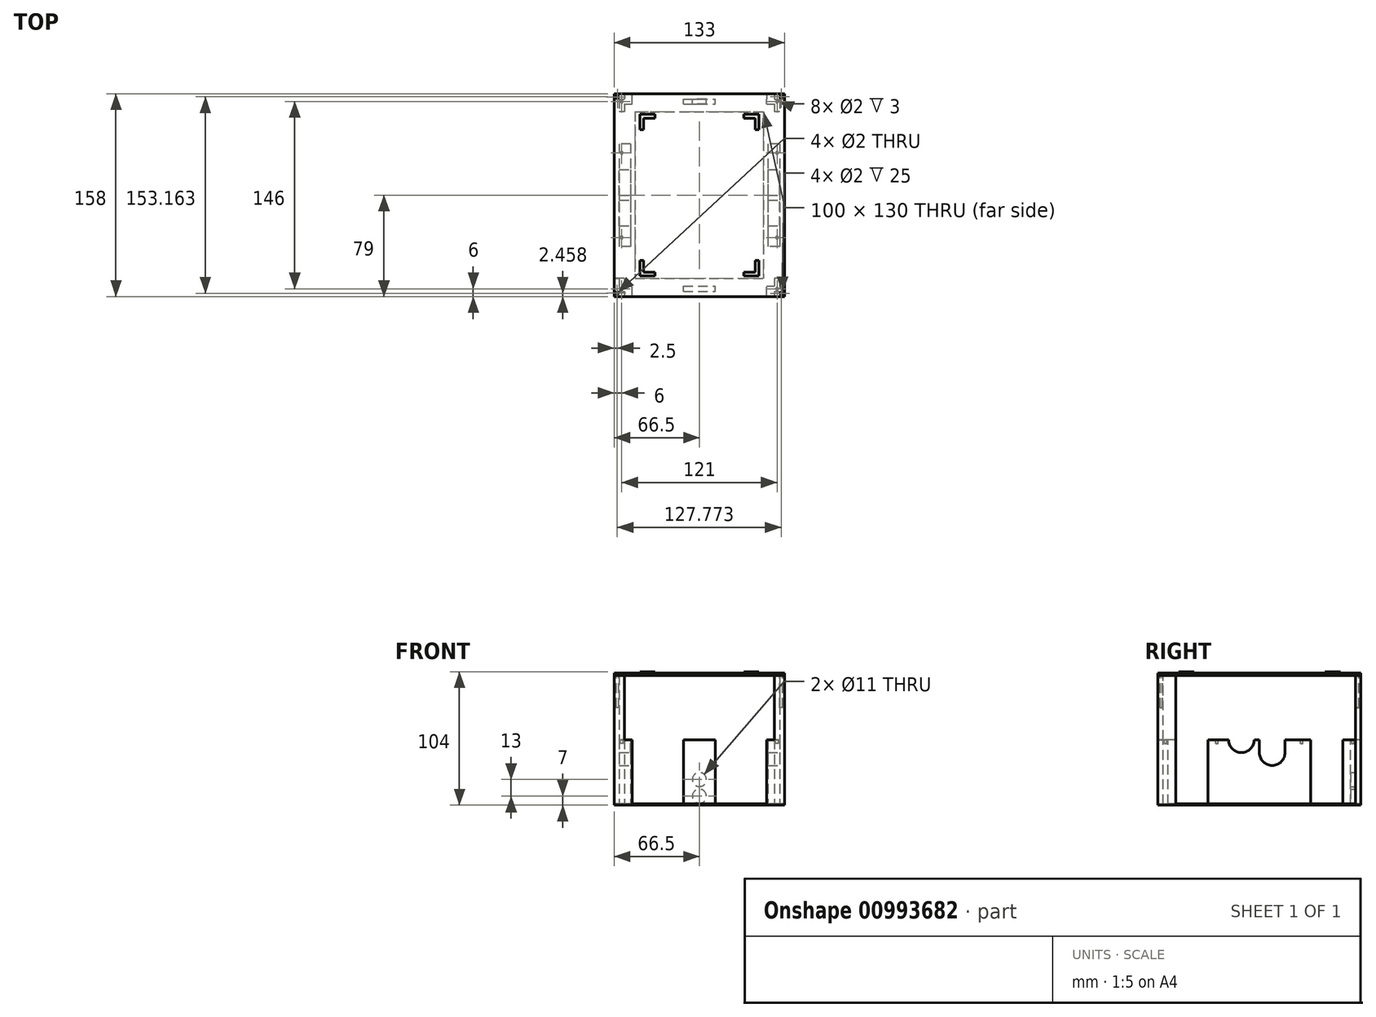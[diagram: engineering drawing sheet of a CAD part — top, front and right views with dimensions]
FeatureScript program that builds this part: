
annotation { "Feature Type Name" : "Feature", "Feature Type Description" : "" }
export const myFeature = defineFeature(function(context is Context, id is Id, definition is map)
    precondition{}
    {
        {
            var Q0;
            Q0=qCreatedBy(makeId("Top.planeOp"),FACE);
            var sketch = newSketch(context, id + "F0", { "sketchPlane" : qUnion([Q0])});
            skLineSegment(sketch, "E0.bottom", {"start": v(-66.5, 79) * mm, "end": v(66.5, 79) * mm});
            skLineSegment(sketch, "E0.top", {"start": v(-66.5, -79) * mm, "end": v(66.5, -79) * mm});
            skLineSegment(sketch, "E0.left", {"start": v(-66.5, 79) * mm, "end": v(-66.5, -79) * mm});
            skLineSegment(sketch, "E0.right", {"start": v(66.5, 79) * mm, "end": v(66.5, -79) * mm});
            skPoint(sketch, "E0.middle", {"position": v(0, 0) * mm});
            skLineSegment(sketch, "E1.bottom", {"start": v(-66.5, 79) * mm, "end": v(-66.5, 79) * mm});
            skLineSegment(sketch, "E1.top", {"start": v(-66.5, 79) * mm, "end": v(-66.5, 79) * mm});
            skLineSegment(sketch, "E1.left", {"start": v(-66.5, 79) * mm, "end": v(-66.5, 79) * mm});
            skLineSegment(sketch, "E1.right", {"start": v(-66.5, 79) * mm, "end": v(-66.5, 79) * mm});
            skLineSegment(sketch, "E2.bottom", {"start": v(-66.5, 79) * mm, "end": v(-62.5, 79) * mm});
            skLineSegment(sketch, "E2.top", {"start": v(-66.5, 79) * mm, "end": v(-62.5, 79) * mm});
            skLineSegment(sketch, "E2.right", {"start": v(-62.5, 79) * mm, "end": v(-62.5, 79) * mm});
            skSolve(sketch);
        }
        {
            var Q0;
            Q0=makeQuery(id+"F0.imprint","IMPRINT",FACE,{"disambiguationData":[TD([[makeQuery(id+"F0.imprint","IMPRINT",EDGE,{"derivedFrom":sQuery(id+"F0.wireOp",EDGE,"E0.bottom")}),-1.0]])]});
            extrude(context, id + "F1", {"entities" : qUnion([Q0]), "depth" : 1 * mm});
        }
        {
            var Q0;
            Q0=makeQuery(id+"F1.opExtrude","CAP_FACE",FACE,{"disambiguationData":[OSD([sQuery(id+"F0.wireOp",EDGE,"E0.bottom"),sQuery(id+"F0.wireOp",EDGE,"E0.top"),sQuery(id+"F0.wireOp",EDGE,"E0.left"),sQuery(id+"F0.wireOp",EDGE,"E0.right")])],"isStart":false});
            var sketch = newSketch(context, id + "F2", { "sketchPlane" : qUnion([Q0])});
            skLineSegment(sketch, "E3.bottom", {"start": v(-62.5, 75) * mm, "end": v(62.5, 75) * mm});
            skLineSegment(sketch, "E3.top", {"start": v(-62.5, -75) * mm, "end": v(62.5, -75) * mm});
            skLineSegment(sketch, "E3.left", {"start": v(-62.5, 75) * mm, "end": v(-62.5, -75) * mm});
            skLineSegment(sketch, "E3.right", {"start": v(62.5, 75) * mm, "end": v(62.5, -75) * mm});
            skPoint(sketch, "E3.middle", {"position": v(0, 0) * mm});
            skSolve(sketch);
        }
        {
            var Q0;
            Q0=qSketchRegion(id+"F2",true);
            extrude(context, id + "F3", {"entities" : qUnion([Q0]), "operationType" : NewBodyOperationType.ADD, "depth" : 50 * mm});
        }
        {
            var Q0;
            Q0=makeQuery(id+"F3.opExtrude","CAP_FACE",FACE,{"disambiguationData":[OSD([sQuery(id+"F2.wireOp",EDGE,"E3.bottom"),sQuery(id+"F2.wireOp",EDGE,"E3.top"),sQuery(id+"F2.wireOp",EDGE,"E3.left"),sQuery(id+"F2.wireOp",EDGE,"E3.right")])],"isStart":false});
            var sketch = newSketch(context, id + "F4", { "sketchPlane" : qUnion([Q0])});
            skLineSegment(sketch, "E4.bottom", {"start": v(-58.5, 71) * mm, "end": v(58.5, 71) * mm});
            skLineSegment(sketch, "E4.top", {"start": v(-58.5, -71) * mm, "end": v(58.5, -71) * mm});
            skLineSegment(sketch, "E4.left", {"start": v(-58.5, 71) * mm, "end": v(-58.5, -71) * mm});
            skLineSegment(sketch, "E4.right", {"start": v(58.5, 71) * mm, "end": v(58.5, -71) * mm});
            skPoint(sketch, "E4.middle", {"position": v(0, 0) * mm});
            skSolve(sketch);
        }
        {
            var Q0;
            Q0=makeQuery(id+"F4.imprint","IMPRINT",FACE,{"disambiguationData":[TD([[makeQuery(id+"F4.imprint","IMPRINT",EDGE,{"derivedFrom":sQuery(id+"F4.wireOp",EDGE,"E4.bottom")}),-1.0]])]});
            extrude(context, id + "F5", {"entities" : qUnion([Q0]), "operationType" : NewBodyOperationType.REMOVE, "oppositeDirection" : true, "depth" : 50 * mm});
        }
        {
            var Q0;
            Q0=makeQuery(id+"F3.opExtrude","CAP_FACE",FACE,{"disambiguationData":[OSD([sQuery(id+"F2.wireOp",EDGE,"E3.bottom"),sQuery(id+"F2.wireOp",EDGE,"E3.top"),sQuery(id+"F2.wireOp",EDGE,"E3.left"),sQuery(id+"F2.wireOp",EDGE,"E3.right")])],"isStart":false});
            var sketch = newSketch(context, id + "F6", { "sketchPlane" : qUnion([Q0])});
            skCircle(sketch, "E5", {"center": v(-60.5, 73) * mm, "radius": 1 * mm});
            skCircle(sketch, "E6", {"center": v(-60.5, 33) * mm, "radius": 1 * mm});
            skCircle(sketch, "E7", {"center": v(60.5, 73) * mm, "radius": 1 * mm});
            skCircle(sketch, "E8", {"center": v(60.5, 33) * mm, "radius": 1 * mm});
            skCircle(sketch, "E9", {"center": v(-60.5, -33) * mm, "radius": 1 * mm});
            skCircle(sketch, "E10", {"center": v(60.5, -33) * mm, "radius": 1 * mm});
            skCircle(sketch, "E11", {"center": v(-60.5, -73) * mm, "radius": 1 * mm});
            skCircle(sketch, "E12", {"center": v(60.5, -73) * mm, "radius": 1 * mm});
            skSolve(sketch);
        }
        {
            var Q0;
            Q0=makeQuery(id+"F6.imprint","IMPRINT",FACE,{"disambiguationData":[TD([[makeQuery(id+"F6.imprint","IMPRINT",EDGE,{"derivedFrom":sQuery(id+"F6.wireOp",EDGE,"E5")}),1.0]])]});
            var Q1;
            Q1=makeQuery(id+"F6.imprint","IMPRINT",FACE,{"disambiguationData":[TD([[makeQuery(id+"F6.imprint","IMPRINT",EDGE,{"derivedFrom":sQuery(id+"F6.wireOp",EDGE,"E7")}),1.0]])]});
            var Q2;
            Q2=makeQuery(id+"F6.imprint","IMPRINT",FACE,{"disambiguationData":[TD([[makeQuery(id+"F6.imprint","IMPRINT",EDGE,{"derivedFrom":sQuery(id+"F6.wireOp",EDGE,"E8")}),1.0]])]});
            var Q3;
            Q3=makeQuery(id+"F6.imprint","IMPRINT",FACE,{"disambiguationData":[TD([[makeQuery(id+"F6.imprint","IMPRINT",EDGE,{"derivedFrom":sQuery(id+"F6.wireOp",EDGE,"E10")}),1.0]])]});
            var Q4;
            Q4=makeQuery(id+"F6.imprint","IMPRINT",FACE,{"disambiguationData":[TD([[makeQuery(id+"F6.imprint","IMPRINT",EDGE,{"derivedFrom":sQuery(id+"F6.wireOp",EDGE,"E12")}),1.0]])]});
            var Q5;
            Q5=makeQuery(id+"F6.imprint","IMPRINT",FACE,{"disambiguationData":[TD([[makeQuery(id+"F6.imprint","IMPRINT",EDGE,{"derivedFrom":sQuery(id+"F6.wireOp",EDGE,"E11")}),1.0]])]});
            var Q6;
            Q6=makeQuery(id+"F6.imprint","IMPRINT",FACE,{"disambiguationData":[TD([[makeQuery(id+"F6.imprint","IMPRINT",EDGE,{"derivedFrom":sQuery(id+"F6.wireOp",EDGE,"E9")}),1.0]])]});
            var Q7;
            Q7=makeQuery(id+"F6.imprint","IMPRINT",FACE,{"disambiguationData":[TD([[makeQuery(id+"F6.imprint","IMPRINT",EDGE,{"derivedFrom":sQuery(id+"F6.wireOp",EDGE,"E6")}),1.0]])]});
            extrude(context, id + "F7", {"entities" : qUnion([Q0, Q1, Q2, Q3, Q4, Q5, Q6, Q7]), "operationType" : NewBodyOperationType.REMOVE, "oppositeDirection" : true, "depth" : 3 * mm});
        }
        {
            var Q0;
            Q0=makeQuery(id+"F3.opExtrude","SWEPT_FACE",FACE,{"disambiguationData":[OSD([sQuery(id+"F2.wireOp",EDGE,"E3.right")])]});
            var sketch = newSketch(context, id + "F8", { "sketchPlane" : qUnion([Q0])});
            skLineSegment(sketch, "E13.bottom", {"start": v(0, 51) * mm, "end": v(20, 51) * mm});
            skLineSegment(sketch, "E13.top", {"start": v(0, 41) * mm, "end": v(20, 41) * mm});
            skLineSegment(sketch, "E13.left", {"start": v(0, 51) * mm, "end": v(0, 41) * mm});
            skLineSegment(sketch, "E13.right", {"start": v(20, 51) * mm, "end": v(20, 41) * mm});
            skSolve(sketch);
        }
        {
            var Q0;
            Q0=makeQuery(id+"F3.opExtrude","SWEPT_FACE",FACE,{"disambiguationData":[OSD([sQuery(id+"F2.wireOp",EDGE,"E3.right")])]});
            var sketch = newSketch(context, id + "F9", { "sketchPlane" : qUnion([Q0])});
            skCircle(sketch, "E14", {"center": v(10, 41) * mm, "radius": 10 * mm});
            skSolve(sketch);
        }
        {
            var Q0;
            Q0=makeQuery(id+"F8.imprint","IMPRINT",FACE,{"disambiguationData":[TD([[makeQuery(id+"F8.imprint","IMPRINT",EDGE,{"derivedFrom":sQuery(id+"F8.wireOp",EDGE,"E13.bottom")}),1.0]])]});
            extrude(context, id + "F10", {"entities" : qUnion([Q0]), "operationType" : NewBodyOperationType.REMOVE, "endBound" : BoundingType.THROUGH_ALL, "oppositeDirection" : true, "depth" : 25 * mm});
        }
        {
            var Q0;
            Q0=makeQuery(id+"F9.imprint","IMPRINT",FACE,{"disambiguationData":[TD([[makeQuery(id+"F9.imprint","IMPRINT",EDGE,{"derivedFrom":sQuery(id+"F9.wireOp",EDGE,"E14")}),1.0]])]});
            extrude(context, id + "F11", {"entities" : qUnion([Q0]), "operationType" : NewBodyOperationType.REMOVE, "endBound" : BoundingType.THROUGH_ALL, "oppositeDirection" : true, "depth" : 25 * mm});
        }
        {
            var Q0;
            Q0=makeQuery(id+"F3.opExtrude","SWEPT_FACE",FACE,{"disambiguationData":[OSD([sQuery(id+"F2.wireOp",EDGE,"E3.right")])]});
            var sketch = newSketch(context, id + "F12", { "sketchPlane" : qUnion([Q0])});
            skCircle(sketch, "E15", {"center": v(-13.97, 51) * mm, "radius": 10 * mm});
            skSolve(sketch);
        }
        {
            var Q0;
            {var subQ0=sQuery(id+"F12.wireOp",EDGE,"E15");var subQ1=sQuery(id+"F2.wireOp",EDGE,"E3.right");var subQ2=sQuery(id+"F2.wireOp",EDGE,"E3.top");var subQ3=makeQuery(id+"F10.boolean.opBoolean","SPLIT",EDGE,{"disambiguationData":[TD([makeQuery(id+"F3.opExtrude","SWEPT_FACE",FACE,{"disambiguationData":[OSD([subQ2])]})])],"derivedFrom":makeQuery(id+"F3.opExtrude","CAP_EDGE",EDGE,{"disambiguationData":[OSD([subQ1])],"isStart":false})});var subQ4=makeQuery(id+"F12.imprint","INTERSECT",VERTEX,{"disambiguationData":[OD(0.0)],"derivedFrom":[subQ3,subQ0]});Q0=makeQuery(id+"F12.imprint","IMPRINT",FACE,{"disambiguationData":[TD([[makeQuery(id+"F12.imprint","IMPRINT",EDGE,{"disambiguationData":[TD([[subQ4,-1.0]])],"derivedFrom":subQ0}),1.0]])]});}
            extrude(context, id + "F13", {"entities" : qUnion([Q0]), "operationType" : NewBodyOperationType.REMOVE, "endBound" : BoundingType.THROUGH_ALL, "oppositeDirection" : true, "depth" : 25 * mm});
        }
        {
            var Q0;
            Q0=makeQuery(id+"F3.opExtrude","SWEPT_FACE",FACE,{"disambiguationData":[OSD([sQuery(id+"F2.wireOp",EDGE,"E3.bottom")])]});
            var sketch = newSketch(context, id + "F14", { "sketchPlane" : qUnion([Q0])});
            skCircle(sketch, "E16", {"center": v(0, 7) * mm, "radius": 5.5 * mm});
            skCircle(sketch, "E17", {"center": v(0, 20) * mm, "radius": 5.5 * mm});
            skSolve(sketch);
        }
        {
            var Q0;
            Q0=makeQuery(id+"F14.imprint","IMPRINT",FACE,{"disambiguationData":[TD([[makeQuery(id+"F14.imprint","IMPRINT",EDGE,{"derivedFrom":sQuery(id+"F14.wireOp",EDGE,"E17")}),1.0]])]});
            var Q1;
            Q1=makeQuery(id+"F14.imprint","IMPRINT",FACE,{"disambiguationData":[TD([[makeQuery(id+"F14.imprint","IMPRINT",EDGE,{"derivedFrom":sQuery(id+"F14.wireOp",EDGE,"E16")}),1.0]])]});
            extrude(context, id + "F15", {"entities" : qUnion([Q0, Q1]), "operationType" : NewBodyOperationType.REMOVE, "oppositeDirection" : true, "depth" : 4 * mm});
        }
        {
            var Q0;
            Q0=makeQuery(id+"F3.opExtrude","SWEPT_FACE",FACE,{"disambiguationData":[OSD([sQuery(id+"F2.wireOp",EDGE,"E3.bottom")])]});
            var sketch = newSketch(context, id + "F16", { "sketchPlane" : qUnion([Q0])});
            skLineSegment(sketch, "E18.bottom", {"start": v(-52.5, 1) * mm, "end": v(-12.5, 1) * mm});
            skLineSegment(sketch, "E18.top", {"start": v(-52.5, 51) * mm, "end": v(-12.5, 51) * mm});
            skLineSegment(sketch, "E18.left", {"start": v(-52.5, 1) * mm, "end": v(-52.5, 51) * mm});
            skLineSegment(sketch, "E18.right", {"start": v(-12.5, 1) * mm, "end": v(-12.5, 51) * mm});
            skLineSegment(sketch, "E19.bottom", {"start": v(12.5, 51) * mm, "end": v(52.5, 51) * mm});
            skLineSegment(sketch, "E19.top", {"start": v(12.5, 1) * mm, "end": v(52.5, 1) * mm});
            skLineSegment(sketch, "E19.left", {"start": v(12.5, 51) * mm, "end": v(12.5, 1) * mm});
            skLineSegment(sketch, "E19.right", {"start": v(52.5, 51) * mm, "end": v(52.5, 1) * mm});
            skSolve(sketch);
        }
        {
            var Q0;
            Q0=makeQuery(id+"F16.imprint","IMPRINT",FACE,{"disambiguationData":[TD([[makeQuery(id+"F16.imprint","IMPRINT",EDGE,{"derivedFrom":sQuery(id+"F16.wireOp",EDGE,"E18.bottom")}),-1.0]])]});
            var Q1;
            Q1=makeQuery(id+"F16.imprint","IMPRINT",FACE,{"disambiguationData":[TD([[makeQuery(id+"F16.imprint","IMPRINT",EDGE,{"derivedFrom":sQuery(id+"F16.wireOp",EDGE,"E19.bottom")}),1.0]])]});
            extrude(context, id + "F17", {"entities" : qUnion([Q0, Q1]), "operationType" : NewBodyOperationType.REMOVE, "endBound" : BoundingType.THROUGH_ALL, "oppositeDirection" : true, "depth" : 25 * mm});
        }
        {
            var Q0;
            Q0=makeQuery(id+"F3.opExtrude","SWEPT_FACE",FACE,{"disambiguationData":[OSD([sQuery(id+"F2.wireOp",EDGE,"E3.left")])]});
            var sketch = newSketch(context, id + "F18", { "sketchPlane" : qUnion([Q0])});
            skLineSegment(sketch, "E20.bottom", {"start": v(-65, 51) * mm, "end": v(-40, 51) * mm});
            skLineSegment(sketch, "E20.top", {"start": v(-65, 1) * mm, "end": v(-40, 1) * mm});
            skLineSegment(sketch, "E20.left", {"start": v(-65, 51) * mm, "end": v(-65, 1) * mm});
            skLineSegment(sketch, "E20.right", {"start": v(-40, 51) * mm, "end": v(-40, 1) * mm});
            skLineSegment(sketch, "E21.bottom", {"start": v(40, 51) * mm, "end": v(65, 51) * mm});
            skLineSegment(sketch, "E21.top", {"start": v(40, 1) * mm, "end": v(65, 1) * mm});
            skLineSegment(sketch, "E21.left", {"start": v(40, 51) * mm, "end": v(40, 1) * mm});
            skLineSegment(sketch, "E21.right", {"start": v(65, 51) * mm, "end": v(65, 1) * mm});
            skSolve(sketch);
        }
        {
            var Q0;
            Q0=makeQuery(id+"F18.imprint","IMPRINT",FACE,{"disambiguationData":[TD([[makeQuery(id+"F18.imprint","IMPRINT",EDGE,{"derivedFrom":sQuery(id+"F18.wireOp",EDGE,"E20.bottom")}),-1.0]])]});
            var Q1;
            Q1=makeQuery(id+"F18.imprint","IMPRINT",FACE,{"disambiguationData":[TD([[makeQuery(id+"F18.imprint","IMPRINT",EDGE,{"derivedFrom":sQuery(id+"F18.wireOp",EDGE,"E21.bottom")}),-1.0]])]});
            extrude(context, id + "F19", {"entities" : qUnion([Q0, Q1]), "operationType" : NewBodyOperationType.REMOVE, "endBound" : BoundingType.THROUGH_ALL, "oppositeDirection" : true, "depth" : 25 * mm});
        }
        {
            var Q0;
            Q0=makeQuery(id+"F19.boolean.opBoolean","MERGE",FACE,{"derivedFrom":[makeQuery(id+"F17.boolean.opBoolean","MERGE",FACE,{"derivedFrom":[makeQuery(id+"F1.opExtrude","CAP_FACE",FACE,{"disambiguationData":[OSD([sQuery(id+"F0.wireOp",EDGE,"E0.bottom"),sQuery(id+"F0.wireOp",EDGE,"E0.top"),sQuery(id+"F0.wireOp",EDGE,"E0.left"),sQuery(id+"F0.wireOp",EDGE,"E0.right"),sQuery(id+"F0.wireOp",EDGE,"E2.top")])],"isStart":false}),makeQuery(id+"F5.boolean.opBoolean","COPY",FACE,{"derivedFrom":makeQuery(id+"F5.opExtrude","CAP_FACE",FACE,{"disambiguationData":[OSD([sQuery(id+"F4.wireOp",EDGE,"E4.bottom"),sQuery(id+"F4.wireOp",EDGE,"E4.top"),sQuery(id+"F4.wireOp",EDGE,"E4.left"),sQuery(id+"F4.wireOp",EDGE,"E4.right")])],"isStart":false})}),makeQuery(id+"F17.opExtrude","SWEPT_FACE",FACE,{"disambiguationData":[OSD([sQuery(id+"F16.wireOp",EDGE,"E18.bottom")])]}),makeQuery(id+"F17.opExtrude","SWEPT_FACE",FACE,{"disambiguationData":[OSD([sQuery(id+"F16.wireOp",EDGE,"E19.top")])]})]}),makeQuery(id+"F19.opExtrude","SWEPT_FACE",FACE,{"disambiguationData":[OSD([sQuery(id+"F18.wireOp",EDGE,"E20.top")])]}),makeQuery(id+"F19.opExtrude","SWEPT_FACE",FACE,{"disambiguationData":[OSD([sQuery(id+"F18.wireOp",EDGE,"E21.top")])]})]});
            var sketch = newSketch(context, id + "F20", { "sketchPlane" : qUnion([Q0])});
            skLineSegment(sketch, "E22.bottom", {"start": v(-66.5, 79) * mm, "end": v(-52.5, 79) * mm});
            skLineSegment(sketch, "E22.top", {"start": v(-66.5, 75) * mm, "end": v(-52.5, 75) * mm});
            skLineSegment(sketch, "E22.left", {"start": v(-66.5, 79) * mm, "end": v(-66.5, 75) * mm});
            skLineSegment(sketch, "E22.right", {"start": v(-52.5, 79) * mm, "end": v(-52.5, 75) * mm});
            skLineSegment(sketch, "E23.bottom", {"start": v(-66.5, 75) * mm, "end": v(-62.5, 75) * mm});
            skLineSegment(sketch, "E23.top", {"start": v(-66.5, 65) * mm, "end": v(-62.5, 65) * mm});
            skLineSegment(sketch, "E23.left", {"start": v(-66.5, 75) * mm, "end": v(-66.5, 65) * mm});
            skLineSegment(sketch, "E23.right", {"start": v(-62.5, 75) * mm, "end": v(-62.5, 65) * mm});
            skLineSegment(sketch, "E24.bottom", {"start": v(52.52, 79) * mm, "end": v(66.5, 79) * mm});
            skLineSegment(sketch, "E24.top", {"start": v(52.52, 75) * mm, "end": v(66.5, 75) * mm});
            skLineSegment(sketch, "E24.left", {"start": v(52.52, 79) * mm, "end": v(52.52, 75) * mm});
            skLineSegment(sketch, "E24.right", {"start": v(66.5, 79) * mm, "end": v(66.5, 75) * mm});
            skLineSegment(sketch, "E25.bottom", {"start": v(62.5, 75) * mm, "end": v(66.5, 75) * mm});
            skLineSegment(sketch, "E25.top", {"start": v(62.5, 64.97) * mm, "end": v(66.5, 64.97) * mm});
            skLineSegment(sketch, "E25.left", {"start": v(62.5, 75) * mm, "end": v(62.5, 64.97) * mm});
            skLineSegment(sketch, "E25.right", {"start": v(66.5, 75) * mm, "end": v(66.5, 64.97) * mm});
            skLineSegment(sketch, "E26.bottom", {"start": v(62.5, -65) * mm, "end": v(66.5, -65) * mm});
            skLineSegment(sketch, "E26.top", {"start": v(62.5, -79) * mm, "end": v(66.5, -79) * mm});
            skLineSegment(sketch, "E26.left", {"start": v(62.5, -65) * mm, "end": v(62.5, -79) * mm});
            skLineSegment(sketch, "E26.right", {"start": v(66.5, -65) * mm, "end": v(66.5, -79) * mm});
            skLineSegment(sketch, "E27.bottom", {"start": v(52.5, -75) * mm, "end": v(62.5, -75) * mm});
            skLineSegment(sketch, "E27.top", {"start": v(52.5, -79) * mm, "end": v(62.5, -79) * mm});
            skLineSegment(sketch, "E27.left", {"start": v(52.5, -75) * mm, "end": v(52.5, -79) * mm});
            skLineSegment(sketch, "E27.right", {"start": v(62.5, -75) * mm, "end": v(62.5, -79) * mm});
            skLineSegment(sketch, "E28.bottom", {"start": v(-66.5, -65) * mm, "end": v(-62.5, -65) * mm});
            skLineSegment(sketch, "E28.top", {"start": v(-66.5, -79) * mm, "end": v(-62.5, -79) * mm});
            skLineSegment(sketch, "E28.left", {"start": v(-66.5, -65) * mm, "end": v(-66.5, -79) * mm});
            skLineSegment(sketch, "E28.right", {"start": v(-62.5, -65) * mm, "end": v(-62.5, -79) * mm});
            skLineSegment(sketch, "E29.bottom", {"start": v(-62.5, -75) * mm, "end": v(-52.5, -75) * mm});
            skLineSegment(sketch, "E29.top", {"start": v(-62.5, -79) * mm, "end": v(-52.5, -79) * mm});
            skLineSegment(sketch, "E29.left", {"start": v(-62.5, -75) * mm, "end": v(-62.5, -79) * mm});
            skLineSegment(sketch, "E29.right", {"start": v(-52.5, -75) * mm, "end": v(-52.5, -79) * mm});
            skSolve(sketch);
        }
        {
            var Q0;
            Q0=makeQuery(id+"F20.imprint","IMPRINT",FACE,{"disambiguationData":[TD([[makeQuery(id+"F20.imprint","IMPRINT",EDGE,{"derivedFrom":sQuery(id+"F20.wireOp",EDGE,"E28.bottom")}),-1.0]])]});
            var Q1;
            Q1=makeQuery(id+"F20.imprint","IMPRINT",FACE,{"disambiguationData":[TD([[makeQuery(id+"F20.imprint","IMPRINT",EDGE,{"derivedFrom":sQuery(id+"F20.wireOp",EDGE,"E29.bottom")}),-1.0]])]});
            var Q2;
            Q2=makeQuery(id+"F20.imprint","IMPRINT",FACE,{"disambiguationData":[TD([[makeQuery(id+"F20.imprint","IMPRINT",EDGE,{"derivedFrom":sQuery(id+"F20.wireOp",EDGE,"E27.bottom")}),-1.0]])]});
            var Q3;
            Q3=makeQuery(id+"F20.imprint","IMPRINT",FACE,{"disambiguationData":[TD([[makeQuery(id+"F20.imprint","IMPRINT",EDGE,{"derivedFrom":sQuery(id+"F20.wireOp",EDGE,"E26.bottom")}),-1.0]])]});
            var Q4;
            Q4=makeQuery(id+"F20.imprint","IMPRINT",FACE,{"disambiguationData":[TD([[makeQuery(id+"F20.imprint","IMPRINT",EDGE,{"derivedFrom":sQuery(id+"F20.wireOp",EDGE,"E22.bottom")}),-1.0]])]});
            var Q5;
            Q5=makeQuery(id+"F20.imprint","IMPRINT",FACE,{"disambiguationData":[TD([[makeQuery(id+"F20.imprint","IMPRINT",EDGE,{"derivedFrom":sQuery(id+"F20.wireOp",EDGE,"E23.bottom")}),-1.0]])]});
            var Q6;
            Q6=makeQuery(id+"F20.imprint","IMPRINT",FACE,{"disambiguationData":[TD([[makeQuery(id+"F20.imprint","IMPRINT",EDGE,{"derivedFrom":sQuery(id+"F20.wireOp",EDGE,"E24.bottom")}),-1.0]])]});
            var Q7;
            {var subQ6=sQuery(id+"F20.wireOp",EDGE,"E25.bottom");Q7=makeQuery(id+"F20.imprint","IMPRINT",FACE,{"disambiguationData":[TD([[makeQuery(id+"F20.imprint","IMPRINT",EDGE,{"derivedFrom":subQ6}),-1.0]])]});}
            extrude(context, id + "F21", {"entities" : qUnion([Q0, Q1, Q2, Q3, Q4, Q5, Q6, Q7]), "operationType" : NewBodyOperationType.ADD, "depth" : 100 * mm});
        }
        {
            var Q0;
            Q0=makeQuery(id+"F21.opExtrude","CAP_FACE",FACE,{"disambiguationData":[OSD([sQuery(id+"F20.wireOp",EDGE,"E22.bottom"),sQuery(id+"F20.wireOp",EDGE,"E22.top"),sQuery(id+"F20.wireOp",EDGE,"E22.left"),sQuery(id+"F20.wireOp",EDGE,"E22.right"),sQuery(id+"F20.wireOp",EDGE,"E23.top"),sQuery(id+"F20.wireOp",EDGE,"E23.left"),sQuery(id+"F20.wireOp",EDGE,"E23.right")])],"isStart":false});
            var sketch = newSketch(context, id + "F22", { "sketchPlane" : qUnion([Q0])});
            skCircle(sketch, "E30", {"center": v(-63.91, 76.41) * mm, "radius": 1 * mm});
            skCircle(sketch, "E31", {"center": v(63.67, 76.62) * mm, "radius": 1 * mm});
            skCircle(sketch, "E32", {"center": v(63.77, -76.54) * mm, "radius": 1 * mm});
            skCircle(sketch, "E33", {"center": v(-64, -76.32) * mm, "radius": 1 * mm});
            skSolve(sketch);
        }
        {
            var Q0;
            Q0=makeQuery(id+"F22.imprint","IMPRINT",FACE,{"disambiguationData":[TD([[makeQuery(id+"F22.imprint","IMPRINT",EDGE,{"derivedFrom":sQuery(id+"F22.wireOp",EDGE,"E30")}),1.0]])]});
            var Q1;
            Q1=makeQuery(id+"F22.imprint","IMPRINT",FACE,{"disambiguationData":[TD([[makeQuery(id+"F22.imprint","IMPRINT",EDGE,{"derivedFrom":sQuery(id+"F22.wireOp",EDGE,"E31")}),1.0]])]});
            var Q2;
            Q2=makeQuery(id+"F22.imprint","IMPRINT",FACE,{"disambiguationData":[TD([[makeQuery(id+"F22.imprint","IMPRINT",EDGE,{"derivedFrom":sQuery(id+"F22.wireOp",EDGE,"E32")}),1.0]])]});
            var Q3;
            Q3=makeQuery(id+"F22.imprint","IMPRINT",FACE,{"disambiguationData":[TD([[makeQuery(id+"F22.imprint","IMPRINT",EDGE,{"derivedFrom":sQuery(id+"F22.wireOp",EDGE,"E33")}),1.0]])]});
            extrude(context, id + "F23", {"entities" : qUnion([Q0, Q1, Q2, Q3]), "operationType" : NewBodyOperationType.REMOVE, "oppositeDirection" : true, "depth" : 25 * mm});
        }
        {
            var Q0;
            {var subQ3=sQuery(id+"F4.wireOp",EDGE,"E4.right");var subQ4=makeQuery(id+"F5.boolean.opBoolean","COPY",FACE,{"derivedFrom":makeQuery(id+"F5.opExtrude","SWEPT_FACE",FACE,{"disambiguationData":[OSD([subQ3])]})});Q0=makeQuery(id+"F19.boolean.opBoolean","SPLIT",FACE,{"disambiguationData":[TD([makeQuery(id+"F19.opExtrude","SWEPT_FACE",FACE,{"disambiguationData":[OSD([sQuery(id+"F18.wireOp",EDGE,"E20.right")])]})])],"derivedFrom":subQ4});}
            extrude(context, id + "F24", {"entities" : qUnion([Q0]), "operationType" : NewBodyOperationType.ADD, "depth" : 5 * mm});
        }
        {
            var Q0;
            {var subQ4=sQuery(id+"F4.wireOp",EDGE,"E4.left");var subQ5=makeQuery(id+"F5.boolean.opBoolean","COPY",FACE,{"derivedFrom":makeQuery(id+"F5.opExtrude","SWEPT_FACE",FACE,{"disambiguationData":[OSD([subQ4])]})});Q0=makeQuery(id+"F19.boolean.opBoolean","SPLIT",FACE,{"disambiguationData":[TD([makeQuery(id+"F19.opExtrude","SWEPT_FACE",FACE,{"disambiguationData":[OSD([sQuery(id+"F18.wireOp",EDGE,"E20.right")])]})])],"derivedFrom":subQ5});}
            extrude(context, id + "F25", {"entities" : qUnion([Q0]), "operationType" : NewBodyOperationType.ADD, "depth" : 5 * mm});
        }
        {
            var Q0;
            Q0=makeQuery(id+"F19.boolean.opBoolean","MERGE",FACE,{"derivedFrom":[makeQuery(id+"F17.boolean.opBoolean","MERGE",FACE,{"derivedFrom":[makeQuery(id+"F1.opExtrude","CAP_FACE",FACE,{"disambiguationData":[OSD([sQuery(id+"F0.wireOp",EDGE,"E0.bottom"),sQuery(id+"F0.wireOp",EDGE,"E0.top"),sQuery(id+"F0.wireOp",EDGE,"E0.left"),sQuery(id+"F0.wireOp",EDGE,"E0.right"),sQuery(id+"F0.wireOp",EDGE,"E2.top")])],"isStart":false}),makeQuery(id+"F5.boolean.opBoolean","COPY",FACE,{"derivedFrom":makeQuery(id+"F5.opExtrude","CAP_FACE",FACE,{"disambiguationData":[OSD([sQuery(id+"F4.wireOp",EDGE,"E4.bottom"),sQuery(id+"F4.wireOp",EDGE,"E4.top"),sQuery(id+"F4.wireOp",EDGE,"E4.left"),sQuery(id+"F4.wireOp",EDGE,"E4.right")])],"isStart":false})}),makeQuery(id+"F17.opExtrude","SWEPT_FACE",FACE,{"disambiguationData":[OSD([sQuery(id+"F16.wireOp",EDGE,"E18.bottom")])]}),makeQuery(id+"F17.opExtrude","SWEPT_FACE",FACE,{"disambiguationData":[OSD([sQuery(id+"F16.wireOp",EDGE,"E19.top")])]})]}),makeQuery(id+"F19.opExtrude","SWEPT_FACE",FACE,{"disambiguationData":[OSD([sQuery(id+"F18.wireOp",EDGE,"E20.top")])]}),makeQuery(id+"F19.opExtrude","SWEPT_FACE",FACE,{"disambiguationData":[OSD([sQuery(id+"F18.wireOp",EDGE,"E21.top")])]})]});
            var sketch = newSketch(context, id + "F26", { "sketchPlane" : qUnion([Q0])});
            skLineSegment(sketch, "E34.bottom", {"start": v(-50, 65) * mm, "end": v(50, 65) * mm});
            skLineSegment(sketch, "E34.top", {"start": v(-50, -65) * mm, "end": v(50, -65) * mm});
            skLineSegment(sketch, "E34.left", {"start": v(-50, 65) * mm, "end": v(-50, -65) * mm});
            skLineSegment(sketch, "E34.right", {"start": v(50, 65) * mm, "end": v(50, -65) * mm});
            skPoint(sketch, "E34.middle", {"position": v(0, 0) * mm});
            skSolve(sketch);
        }
        {
            var Q0;
            Q0=makeQuery(id+"F26.imprint","IMPRINT",FACE,{"disambiguationData":[TD([[makeQuery(id+"F26.imprint","IMPRINT",EDGE,{"derivedFrom":sQuery(id+"F26.wireOp",EDGE,"E34.bottom")}),-1.0]])]});
            extrude(context, id + "F27", {"entities" : qUnion([Q0]), "operationType" : NewBodyOperationType.REMOVE, "endBound" : BoundingType.THROUGH_ALL, "oppositeDirection" : true, "depth" : 25 * mm});
        }
        {
            var Q0;
            Q0=makeQuery(id+"F21.boolean.opBoolean","MERGE",FACE,{"derivedFrom":[makeQuery(id+"F1.opExtrude","SWEPT_FACE",FACE,{"disambiguationData":[OSD([sQuery(id+"F0.wireOp",EDGE,"E0.top")])]}),makeQuery(id+"F21.opExtrude","SWEPT_FACE",FACE,{"disambiguationData":[OSD([sQuery(id+"F20.wireOp",EDGE,"E26.top"),sQuery(id+"F20.wireOp",EDGE,"E27.top")])]}),makeQuery(id+"F21.opExtrude","SWEPT_FACE",FACE,{"disambiguationData":[OSD([sQuery(id+"F20.wireOp",EDGE,"E28.top"),sQuery(id+"F20.wireOp",EDGE,"E29.top")])]})]});
            var sketch = newSketch(context, id + "F28", { "sketchPlane" : qUnion([Q0])});
            skLineSegment(sketch, "E35.bottom", {"start": v(-52.5, 101) * mm, "end": v(-58.5, 101) * mm});
            skLineSegment(sketch, "E35.top", {"start": v(-52.5, 51) * mm, "end": v(-58.5, 51) * mm});
            skLineSegment(sketch, "E35.left", {"start": v(-52.5, 101) * mm, "end": v(-52.5, 51) * mm});
            skLineSegment(sketch, "E35.right", {"start": v(-58.5, 101) * mm, "end": v(-58.5, 51) * mm});
            skLineSegment(sketch, "E36.bottom", {"start": v(52.5, 101) * mm, "end": v(58.5, 101) * mm});
            skLineSegment(sketch, "E36.top", {"start": v(52.5, 51) * mm, "end": v(58.5, 51) * mm});
            skLineSegment(sketch, "E36.left", {"start": v(52.5, 101) * mm, "end": v(52.5, 51) * mm});
            skLineSegment(sketch, "E36.right", {"start": v(58.5, 101) * mm, "end": v(58.5, 51) * mm});
            skSolve(sketch);
        }
        {
            var Q0;
            Q0=makeQuery(id+"F28.imprint","IMPRINT",FACE,{"disambiguationData":[TD([[makeQuery(id+"F28.imprint","IMPRINT",EDGE,{"derivedFrom":sQuery(id+"F28.wireOp",EDGE,"E35.bottom")}),-1.0]])]});
            var Q1;
            Q1=makeQuery(id+"F28.imprint","IMPRINT",FACE,{"disambiguationData":[TD([[makeQuery(id+"F28.imprint","IMPRINT",EDGE,{"derivedFrom":sQuery(id+"F28.wireOp",EDGE,"E36.bottom")}),-1.0]])]});
            extrude(context, id + "F29", {"entities" : qUnion([Q0, Q1]), "operationType" : NewBodyOperationType.REMOVE, "endBound" : BoundingType.THROUGH_ALL, "oppositeDirection" : true, "depth" : 25 * mm});
        }
        {
            var Q0;
            Q0=makeQuery(id+"F21.opExtrude","CAP_FACE",FACE,{"disambiguationData":[OSD([sQuery(id+"F20.wireOp",EDGE,"E28.bottom"),sQuery(id+"F20.wireOp",EDGE,"E28.top"),sQuery(id+"F20.wireOp",EDGE,"E28.left"),sQuery(id+"F20.wireOp",EDGE,"E28.right"),sQuery(id+"F20.wireOp",EDGE,"E29.bottom"),sQuery(id+"F20.wireOp",EDGE,"E29.top"),sQuery(id+"F20.wireOp",EDGE,"E29.right")])],"isStart":false});
            cPlane(context, id + "F30", {"entities" : qUnion([Q0]), "cplaneType" : CPlaneType.OFFSET, "offset" : 0 * mm, "width" : 150 * mm, "height" : 150 * mm});
        }
        {
            var Q0;
            Q0=qCreatedBy(id+"F30.planeOp",FACE);
            var sketch = newSketch(context, id + "F31", { "sketchPlane" : qUnion([Q0])});
            skLineSegment(sketch, "E37", {"start": v(-66.5, 79) * mm, "end": v(66.5, 79) * mm});
            skLineSegment(sketch, "E38", {"start": v(66.5, -79) * mm, "end": v(-66.5, -79) * mm});
            skLineSegment(sketch, "E39", {"start": v(-66.5, -79) * mm, "end": v(-66.5, 79) * mm});
            skLineSegment(sketch, "E40", {"start": v(66.5, 79) * mm, "end": v(66.5, -79) * mm});
            skCircle(sketch, "E41.0", {"center": v(-63.91, 76.41) * mm, "radius": 1 * mm});
            skCircle(sketch, "E41.1", {"center": v(63.67, 76.62) * mm, "radius": 1 * mm});
            skCircle(sketch, "E41.2", {"center": v(-64, -76.32) * mm, "radius": 1 * mm});
            skCircle(sketch, "E41.3", {"center": v(63.77, -76.54) * mm, "radius": 1 * mm});
            skPoint(sketch, "E42.middle", {"position": v(0, 0) * mm});
            skLineSegment(sketch, "E43", {"start": v(-43.5, 51) * mm, "end": v(-46.5, 51) * mm});
            skLineSegment(sketch, "E44", {"start": v(-46.5, 51) * mm, "end": v(-46.5, 63) * mm});
            skLineSegment(sketch, "E45", {"start": v(-46.5, 63) * mm, "end": v(-34.5, 63) * mm});
            skLineSegment(sketch, "E46", {"start": v(-34.5, 63) * mm, "end": v(-34.5, 60) * mm});
            skLineSegment(sketch, "E47", {"start": v(-34.5, 60) * mm, "end": v(-43.5, 60) * mm});
            skLineSegment(sketch, "E48", {"start": v(-43.5, 60) * mm, "end": v(-43.5, 51) * mm});
            skLineSegment(sketch, "E49.MirrorCS", {"start": v(46.5, 63) * mm, "end": v(34.5, 63) * mm});
            skLineSegment(sketch, "E50.MirrorCS", {"start": v(46.5, 51) * mm, "end": v(46.5, 63) * mm});
            skLineSegment(sketch, "E51.MirrorCS", {"start": v(43.5, 51) * mm, "end": v(46.5, 51) * mm});
            skLineSegment(sketch, "E52.MirrorCS", {"start": v(43.5, 60) * mm, "end": v(43.5, 51) * mm});
            skLineSegment(sketch, "E53.MirrorCS", {"start": v(34.5, 60) * mm, "end": v(43.5, 60) * mm});
            skLineSegment(sketch, "E54.MirrorCS", {"start": v(34.5, 63) * mm, "end": v(34.5, 60) * mm});
            skLineSegment(sketch, "E55.MirrorCS", {"start": v(-34.5, -63) * mm, "end": v(-34.5, -60) * mm});
            skLineSegment(sketch, "E56.MirrorCS", {"start": v(43.5, -51) * mm, "end": v(46.5, -51) * mm});
            skLineSegment(sketch, "E57.MirrorCS", {"start": v(-43.5, -51) * mm, "end": v(-46.5, -51) * mm});
            skLineSegment(sketch, "E58.MirrorCS", {"start": v(34.5, -63) * mm, "end": v(34.5, -60) * mm});
            skLineSegment(sketch, "E59.MirrorCS", {"start": v(-46.5, -51) * mm, "end": v(-46.5, -63) * mm});
            skLineSegment(sketch, "E60.MirrorCS", {"start": v(-43.5, -60) * mm, "end": v(-43.5, -51) * mm});
            skLineSegment(sketch, "E61.MirrorCS", {"start": v(43.5, -60) * mm, "end": v(43.5, -51) * mm});
            skLineSegment(sketch, "E62.MirrorCS", {"start": v(-46.5, -63) * mm, "end": v(-34.5, -63) * mm});
            skLineSegment(sketch, "E63.MirrorCS", {"start": v(46.5, -63) * mm, "end": v(34.5, -63) * mm});
            skLineSegment(sketch, "E64.MirrorCS", {"start": v(-34.5, -60) * mm, "end": v(-43.5, -60) * mm});
            skLineSegment(sketch, "E65.MirrorCS", {"start": v(46.5, -51) * mm, "end": v(46.5, -63) * mm});
            skLineSegment(sketch, "E66.MirrorCS", {"start": v(34.5, -60) * mm, "end": v(43.5, -60) * mm});
            skSolve(sketch);
        }
        {
            var Q0;
            Q0=makeQuery(id+"F31.imprint","IMPRINT",FACE,{"disambiguationData":[TD([[makeQuery(id+"F31.imprint","IMPRINT",EDGE,{"derivedFrom":sQuery(id+"F31.wireOp",EDGE,"E37")}),-1.0]])]});
            extrude(context, id + "F32", {"entities" : qUnion([Q0]), "depth" : 2 * mm, "offsetDistance" : 25 * mm});
        }
        {
            var Q0;
            Q0=makeQuery(id+"F31.imprint","IMPRINT",FACE,{"disambiguationData":[TD([[makeQuery(id+"F31.imprint","IMPRINT",EDGE,{"derivedFrom":sQuery(id+"F31.wireOp",EDGE,"E43")}),-1.0]])]});
            var Q1;
            Q1=makeQuery(id+"F31.imprint","IMPRINT",FACE,{"disambiguationData":[TD([[makeQuery(id+"F31.imprint","IMPRINT",EDGE,{"derivedFrom":sQuery(id+"F31.wireOp",EDGE,"E49.MirrorCS")}),1.0]])]});
            var Q2;
            Q2=makeQuery(id+"F31.imprint","IMPRINT",FACE,{"disambiguationData":[TD([[makeQuery(id+"F31.imprint","IMPRINT",EDGE,{"derivedFrom":sQuery(id+"F31.wireOp",EDGE,"E55.MirrorCS")}),1.0]])]});
            var Q3;
            Q3=makeQuery(id+"F31.imprint","IMPRINT",FACE,{"disambiguationData":[TD([[makeQuery(id+"F31.imprint","IMPRINT",EDGE,{"derivedFrom":sQuery(id+"F31.wireOp",EDGE,"E56.MirrorCS")}),-1.0]])]});
            extrude(context, id + "F33", {"entities" : qUnion([Q0, Q1, Q2, Q3]), "operationType" : NewBodyOperationType.ADD, "depth" : 3 * mm, "offsetDistance" : 25 * mm});
        }
    });
